# Revit family: IVLB_L4U_LF_Track Spot - EDDA M
name_source: partatom
category: Lighting Fixtures
units: mm (PartAtom-declared; Revit-internal decimal feet)

## family parameters
Always vertical = No
Cut with Voids When Loaded = No
Light Source = No
Part Type = Normal
Room Calculation Point = No
Round Connector Dimension = Use Diameter
Shared = No
Work Plane-Based = No

## types (12) — shared parameters
Assembly Code = 63.00
Calc_Coupling_Length = 41 mm  [stored 0.134514 ft]
Description = Track Spot Edda M
IfcExportAs = IfcLightFixtureType
IfcExportType = POINTSOURCE
Lamp = LED
Manufacturer = Light4U
Model = Track Spot Edda M
Track Adapter_Height = 30 mm  [stored 0.0984252 ft]
Track Adapter_Length = 228 mm  [stored 0.748031 ft]
Track Adapter_Width = 29 mm  [stored 0.0951444 ft]
Track_Spot_Diameter = 96 mm  [stored 0.314961 ft]
Track_Spot_Length = 112 mm  [stored 0.367454 ft]
Track_Spot_Position_LR = 55 mm  [stored 0.180446 ft]
Track_Spot_Position_UD = 41 mm  [stored 0.134514 ft]
Type Comments = Edda M
URL = https://light4u.io
⌂ Powered by IVLibrary = www.ivlibrary.com

## per-type parameters (varying)
| type | Apparent Load | Light Source | Wattage Comments |
| EDDA M 1450lm_930 14W 30deg | 14 VA | Lightsource M : EDDA M 1450lm_930 14.5W 30deg_LDT | 14W |
| EDDA M 1450lm_930 14W 20deg | 14 VA | Lightsource M : EDDA M 1450lm_930 14W 20deg_LDT | 14W |
| EDDA M 1450lm_930 14W 45deg | 14 VA | Lightsource M : EDDA M 1450lm_930 14W 45deg_LDT | 14W |
| EDDA M 1450lm_930 14W 55deg | 14 VA | Lightsource M : EDDA M 1450lm_930 14W 55deg_LDT | 14W |
| EDDA M 2000lm_930 18.5W 20deg | 19 VA | Lightsource M : EDDA M 2000lm_930 18.5W 20deg_LDT | 18.5W |
| EDDA M 2000lm_930 18.5W 30deg | 19 VA | Lightsource M : EDDA M 2000lm_930 18.5W 30deg_LDT | 18.5W |
| EDDA M 2000lm_930 18.5W 45deg | 19 VA | Lightsource M : EDDA M 2000lm_930 18.5W 45deg_LDT | 18.5W |
| EDDA M 2000lm_930 18.5W 55deg | 19 VA | Lightsource M : EDDA M 2000lm_930 18.5W 55deg_LDT | 18.5W |
| EDDA M 3000lm_930 30W 20deg | 30 VA | Lightsource M : EDDA M 3000lm_930 30W 20deg_LDT | 30W |
| EDDA M 3000lm_930 30W 30deg | 30 VA | Lightsource M : EDDA M 3000lm_930 30W 30deg_LDT | 30W |
| EDDA M 3000lm_930 30W 45deg | 30 VA | Lightsource M : EDDA M 3000lm_930 30W 45deg_LDT | 30W |
| EDDA M 3000lm_930 30W 55deg | 30 VA | Lightsource M : EDDA M 3000lm_930 30W 55deg_LDT | 30W |

note: [stored X ft] marks values corroborated as IEEE doubles in the binary element streams (Revit-internal decimal feet)

## geometry (parser evidence)
native form markers: Sweep x17
no freeform markers — native parametric forms only
